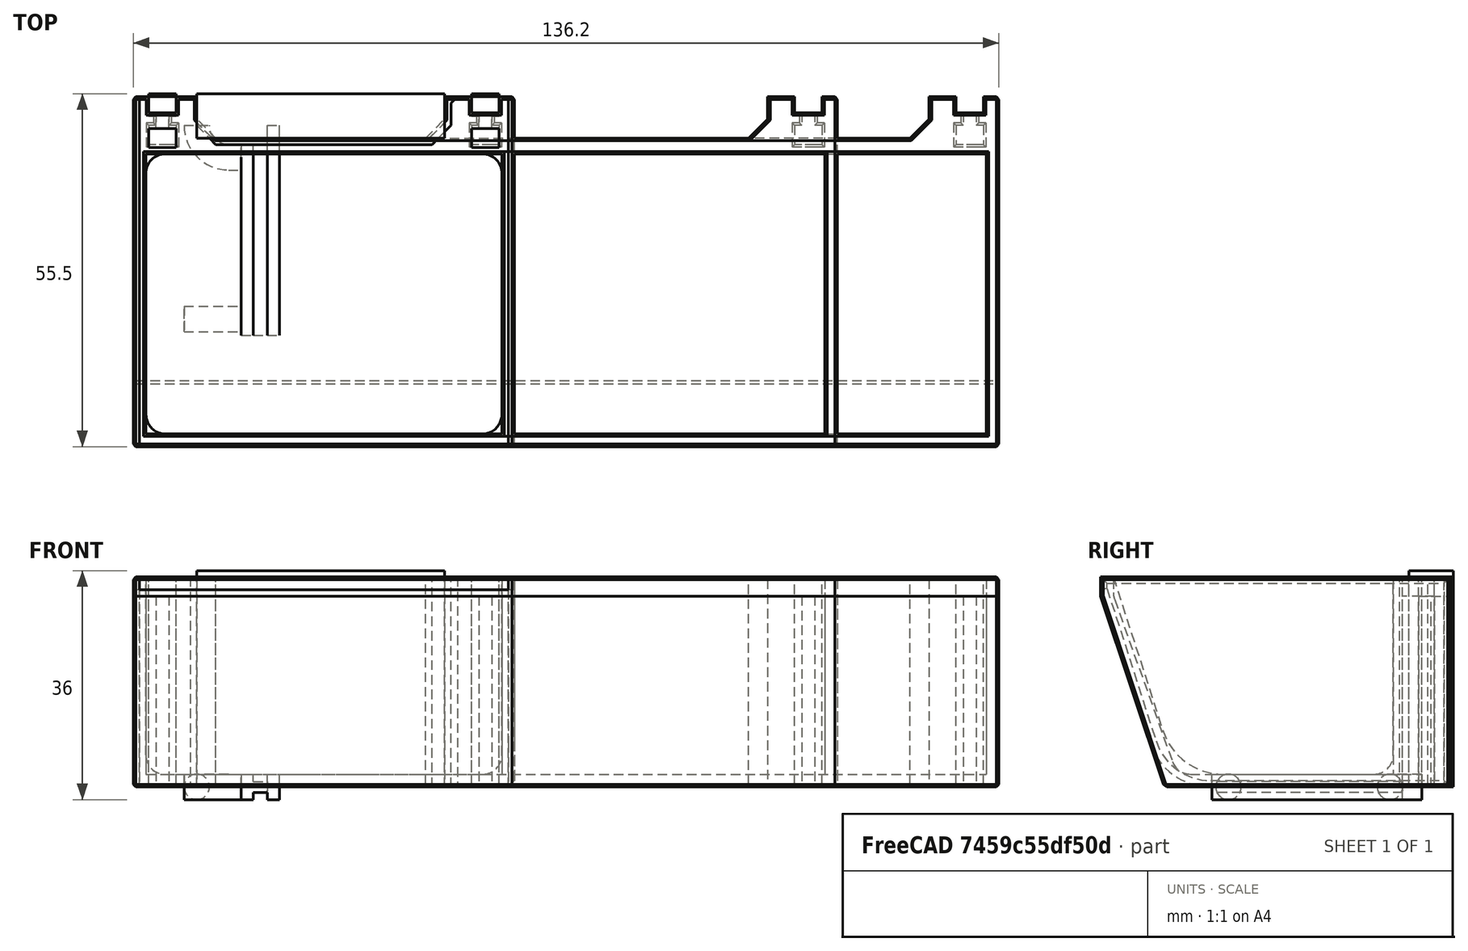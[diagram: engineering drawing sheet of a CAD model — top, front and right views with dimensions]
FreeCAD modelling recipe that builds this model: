
FCSTD DOCUMENT  (FreeCAD 0.19R24291 (Git))
Label: peg-bard-part-tray-3slot
License: Other
LicenseURL: GPL3
objects: Part::Feature×19, Part::Chamfer×11, Part::Cut×11, Part::Box×7, Part::Extrusion×6, Part::MultiFuse×4, Part::Fillet×3
note: 61 computed .brp shape members not serialized (recipe doc carries the construction recipe); baked Part::Feature solids carry a one-line shape summary decoded from their .brp

FEATURE [Part::Feature] Fusion001001001  label="mounter-slot001"
  Placement = pos=(-25.4,10,0) rot=(0,0,1;3.14159rad)
  shape: bbox 4.3 x 8 x 33 mm, 26 faces (baked)
FEATURE [Part::Feature] Fusion001001002  label="mounter-slot002"
  Placement = pos=(25.4,10,0) rot=(0,0,1;3.14159rad)
  shape: bbox 4.3 x 8 x 33 mm, 26 faces (baked)
FEATURE [Part::Box] Box  label="Cube"
  AttacherType = Attacher::AttachEngine3D
  Height = 33
  Length = 60
  Placement = pos=(-30,-45.5,0) rot=(0,0,1;0rad)
  Width = 55
FEATURE [Part::Box] Box001  label="Cube001"
  AttacherType = Attacher::AttachEngine3D
  Height = 32
  Length = 56
  Placement = pos=(-28,-43.5,2) rot=(0,0,1;0rad)
  Width = 44
FEATURE [Part::Chamfer] Chamfer001
  Base = -> Box
  Edges = 1 edges: [Edge9 r1=31 r2=10]
FEATURE [Part::Fillet] Fillet001
  Base = -> Chamfer001
  Edges = 1 edges r=10: [Edge9]
FEATURE [Part::Box] Box002  label="Cube002"
  AttacherType = Attacher::AttachEngine3D
  Height = 38
  Length = 40
  Placement = pos=(-20,2,0) rot=(0,0,1;0rad)
  Width = 10
FEATURE [Part::MultiFuse] Fusion
  Placement = pos=(1e-15,11.5,0) rot=(0,0,1;3.14159rad)
  Shapes = -> [Fusion001001002,Fusion001001001]
FEATURE [Part::Chamfer] Chamfer
  Base = -> Box001
  Edges = 1 edges: [Edge9 r1=31 r2=10]
FEATURE [Part::Fillet] Fillet
  Base = -> Chamfer
  Edges = 1 edges r=10: [Edge9]
FEATURE [Part::Cut] Cut
  Base = -> Fillet001
  Tool = -> Fillet
FEATURE [Part::Fillet] Fillet002
  Base = -> Cut
  Edges = 9 edges r=3: [Edge23,Edge25,Edge26,Edge27,Edge28,Edge29,Edge30,Edge31,Edge32]
FEATURE [Part::Chamfer] Chamfer002
  Base = -> Fillet002
  Edges = 12 edges r=1: [Edge9,Edge12,Edge31,Edge32,Edge33,Edge34,Edge35,Edge37,Edge38,Edge40,Edge41,Edge42]
FEATURE [Part::Cut] Cut001
  Base = -> Chamfer002
  Tool = -> Box002
FEATURE [Part::Chamfer] Chamfer003
  Base = -> Cut001
  Edges = 2 edges r=3: [Edge20,Edge22]
FEATURE [Part::Chamfer] Chamfer004
  Base = -> Chamfer003
  Edges = 2 edges r=1: [Edge20,Edge36]
FEATURE [Part::Cut] Cut002
  Base = -> Chamfer004
  Tool = -> Fusion
FEATURE [Part::Feature] Fusion001001003  label="mounter-slot003"
  Placement = pos=(25.4,10,0) rot=(0,0,1;3.14159rad)
  shape: bbox 4.3 x 8 x 33 mm, 26 faces (baked)
FEATURE [Part::Feature] Fusion001001004  label="mounter-slot004"
  Placement = pos=(-25.4,10,0) rot=(0,0,1;3.14159rad)
  shape: bbox 4.3 x 8 x 33 mm, 26 faces (baked)
FEATURE [Part::Feature] Fillet004001_cs  label="inner-template"
  Placement = pos=(-28,0,0) rot=(0,0,1;0rad)
  shape: bbox 3e-07 x 44 x 31 mm, 0 faces, 0 solids (baked)
FEATURE [Part::Feature] Chamfer006001_cs  label="outer-template"
  Placement = pos=(-30,0,0) rot=(0,0,1;0rad)
  shape: bbox 3e-07 x 55 x 33 mm, 0 faces, 0 solids (baked)
FEATURE [Part::Feature] Chamfer006001_cs001  label="outer-template001"
  Placement = pos=(-30,0,0) rot=(0,0,1;0rad)
  shape: bbox 3e-07 x 55 x 33 mm, 0 faces, 0 solids (baked)
FEATURE [Part::Feature] Fillet004001_cs001  label="inner-template001"
  Placement = pos=(-28,0,0) rot=(0,0,1;0rad)
  shape: bbox 3e-07 x 44 x 31 mm, 0 faces, 0 solids (baked)
FEATURE [Part::Extrusion] Extrude
  Base = -> Chamfer006001_cs001
  Dir = (1,0,0)
  DirMode = 2
  FaceMakerClass = Part::FaceMakerBullseye
  LengthFwd = 60
  LengthRev = 0
  Solid = true
  Symmetric = false
FEATURE [Part::Extrusion] Extrude001
  Base = -> Fillet004001_cs001
  Dir = (1,0,0)
  DirMode = 2
  FaceMakerClass = Part::FaceMakerBullseye
  LengthFwd = 56
  LengthRev = 0
  Solid = true
  Symmetric = false
FEATURE [Part::Cut] Cut003
  Base = -> Extrude
  Tool = -> Extrude001
FEATURE [Part::Feature] Fusion001001005  label="mounter-slot005"
  Placement = pos=(-25.4,10,0) rot=(0,0,1;3.14159rad)
  shape: bbox 4.3 x 8 x 33 mm, 26 faces (baked)
FEATURE [Part::Feature] Fusion001001006  label="mounter-slot006"
  Placement = pos=(25.4,10,0) rot=(0,0,1;3.14159rad)
  shape: bbox 4.3 x 8 x 33 mm, 26 faces (baked)
FEATURE [Part::MultiFuse] Fusion001001007
  Shapes = -> [Fusion001001006,Fusion001001005]
FEATURE [Part::Cut] Cut004
  Base = -> Cut003
  Tool = -> Fusion001001007
FEATURE [Part::Box] Box003  label="Cube003"
  AttacherType = Attacher::AttachEngine3D
  Height = 34
  Length = 39
  Placement = pos=(-20,3,0) rot=(0,0,1;0rad)
  Width = 7
FEATURE [Part::Box] Box004  label="Cube004"
  AttacherType = Attacher::AttachEngine3D
  Height = 34
  Length = 39
  Placement = pos=(-20,3,0) rot=(0,0,1;0rad)
  Width = 7
FEATURE [Part::Chamfer] Chamfer005
  Base = -> Box004
  Edges = 2 edges r=3: [Edge1,Edge5]
FEATURE [Part::Cut] Cut005
  Base = -> Cut004
  Tool = -> Chamfer005
FEATURE [Part::Chamfer] Chamfer006  label="w2-tray"
  Base = -> Cut005
  Edges = 66 edges r=0.4: [Edge1,Edge2,Edge3,Edge4,Edge5,Edge6,Edge7,Edge8,Edge9,Edge10,Edge11,Edge12,Edge13,Edge14,Edge15,Edge16,Edge17,Edge18,Edge19,Edge20,Edge21,Edge22,Edge23,Edge24,Edge25,Edge26,Edge27,Edge30,Edge31,Edge35,Edge37,Edge39,Edge41,Edge43,Edge45,Edge47,Edge50,Edge51,Edge54,Edge55,Edge59,Edge61,Edge63,Edge64,+22 more]
FEATURE [Part::Feature] Chamfer006001_cs002  label="outer-template002"
  Placement = pos=(-30,0,0) rot=(0,0,1;0rad)
  shape: bbox 3e-07 x 55 x 33 mm, 0 faces, 0 solids (baked)
FEATURE [Part::Feature] Fillet004001_cs002  label="inner-template002"
  Placement = pos=(-28,0,0) rot=(0,0,1;0rad)
  shape: bbox 3e-07 x 44 x 31 mm, 0 faces, 0 solids (baked)
FEATURE [Part::Extrusion] Extrude002
  Base = -> Chamfer006001_cs002
  Dir = (1,0,0)
  DirMode = 2
  FaceMakerClass = Part::FaceMakerBullseye
  LengthFwd = 136.2
  LengthRev = 0
  Solid = true
  Symmetric = false
FEATURE [Part::Extrusion] Extrude003
  Base = -> Fillet004001_cs002
  Dir = (1,0,0)
  DirMode = 2
  FaceMakerClass = Part::FaceMakerBullseye
  LengthFwd = 132.2
  LengthRev = 0
  Solid = true
  Symmetric = false
FEATURE [Part::Cut] Cut006
  Base = -> Extrude002
  Tool = -> Extrude003
FEATURE [Part::Box] Box005  label="Cube005"
  AttacherType = Attacher::AttachEngine3D
  Height = 34
  Length = 115.2
  Placement = pos=(-20,3,0) rot=(0,0,1;0rad)
  Width = 7
FEATURE [Part::Chamfer] Chamfer007
  Base = -> Box005
  Edges = 2 edges r=3: [Edge1,Edge5]
FEATURE [Part::Cut] Cut007
  Base = -> Cut006
  Tool = -> Chamfer007
FEATURE [Part::Feature] Fusion001001008  label="mounter-slot007"
  Placement = pos=(101.6,10,0) rot=(0,0,1;3.14159rad)
  shape: bbox 4.3 x 8 x 33 mm, 26 faces (baked)
FEATURE [Part::Feature] Fusion001001009  label="mounter-slot008"
  Placement = pos=(-25.4,10,0) rot=(0,0,1;3.14159rad)
  shape: bbox 4.3 x 8 x 33 mm, 26 faces (baked)
FEATURE [Part::MultiFuse] Fusion001001010
  Shapes = -> [Fusion001001008,Fusion001001009]
FEATURE [Part::Cut] Cut008
  Base = -> Cut007
  Tool = -> Fusion001001010
FEATURE [Part::Chamfer] Chamfer008  label="w5-tray"
  Base = -> Cut008
  Edges = <same value as first occurrence — deduplicated (x3 in doc)>
FEATURE [Part::Feature] Fusion001002004003010003009005001  label="hook"
  shape: bbox 15.58 x 33 x 4 mm, 22 faces (baked)
FEATURE [Part::Box] Box006  label="Cube006"
  AttacherType = Attacher::AttachEngine3D
  Height = 34
  Length = 89.8
  Placement = pos=(-20,3,0) rot=(0,0,1;0rad)
  Width = 7
FEATURE [Part::Feature] Chamfer006001_cs003  label="outer-template003"
  Placement = pos=(-30,0,0) rot=(0,0,1;0rad)
  shape: bbox 3e-07 x 55 x 33 mm, 0 faces, 0 solids (baked)
FEATURE [Part::Feature] Fillet004001_cs003  label="inner-template003"
  Placement = pos=(-28,0,0) rot=(0,0,1;0rad)
  shape: bbox 3e-07 x 44 x 31 mm, 0 faces, 0 solids (baked)
FEATURE [Part::Feature] Fusion001002004003010003009005002  label="mounter-slot009"
  Placement = pos=(-25.4,10,0) rot=(0,0,1;3.14159rad)
  shape: bbox 4.3 x 8 x 33 mm, 26 faces (baked)
FEATURE [Part::Feature] Fusion001002004003010003009005003  label="mounter-slot010"
  Placement = pos=(76.2,10,0) rot=(0,0,1;3.14159rad)
  shape: bbox 4.3 x 8 x 33 mm, 26 faces (baked)
FEATURE [Part::Extrusion] Extrude004
  Base = -> Chamfer006001_cs003
  Dir = (1,0,0)
  DirMode = 2
  FaceMakerClass = Part::FaceMakerBullseye
  LengthFwd = 110.8
  LengthRev = 0
  Solid = true
  Symmetric = false
FEATURE [Part::Extrusion] Extrude005
  Base = -> Fillet004001_cs003
  Dir = (1,0,0)
  DirMode = 2
  FaceMakerClass = Part::FaceMakerBullseye
  LengthFwd = 106.8
  LengthRev = 0
  Solid = true
  Symmetric = false
FEATURE [Part::Chamfer] Chamfer009
  Base = -> Box006
  Edges = 2 edges r=3: [Edge1,Edge5]
FEATURE [Part::MultiFuse] Fusion001002004003010003009005004
  Shapes = -> [Fusion001002004003010003009005002,Fusion001002004003010003009005003,Chamfer009]
FEATURE [Part::Cut] Cut009
  Base = -> Extrude004
  Tool = -> Extrude005
FEATURE [Part::Cut] Cut010
  Base = -> Cut009
  Tool = -> Fusion001002004003010003009005004
FEATURE [Part::Chamfer] Chamfer010
  Base = -> Cut010
  Edges = <same value as first occurrence — deduplicated (x3 in doc)>
